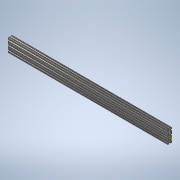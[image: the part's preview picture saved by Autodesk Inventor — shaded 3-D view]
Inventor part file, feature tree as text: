
AUTODESK INVENTOR PART (.ipt)
format: ipt  version: 2020 (Build 240168000, 168)  size: 398,336 bytes
history: native  units: in
note: dims shown in document units (in); Inventor stores cm internally (conversion verified against a paired STEP export)
features: sketch x2, extrude x1
ambient origin geometry x8: Origin, YZ Plane, XZ Plane, XY Plane, X Axis, Y Axis, Z Axis, Center Point
bodies: Solid1 (feature_tree)
feature tree (3):
  extrude  "Extrusion1"  [1 undecoded]
  sketch  "Sketch2"
  sketch  "Sketch1"  dims[d0=36.0in d1=0.0in]
note: 1 required parameter value undecoded (feature->parameter linkage not recoverable at this tier; creation-order binding heuristic only, values carry confidence <= 0.55)
